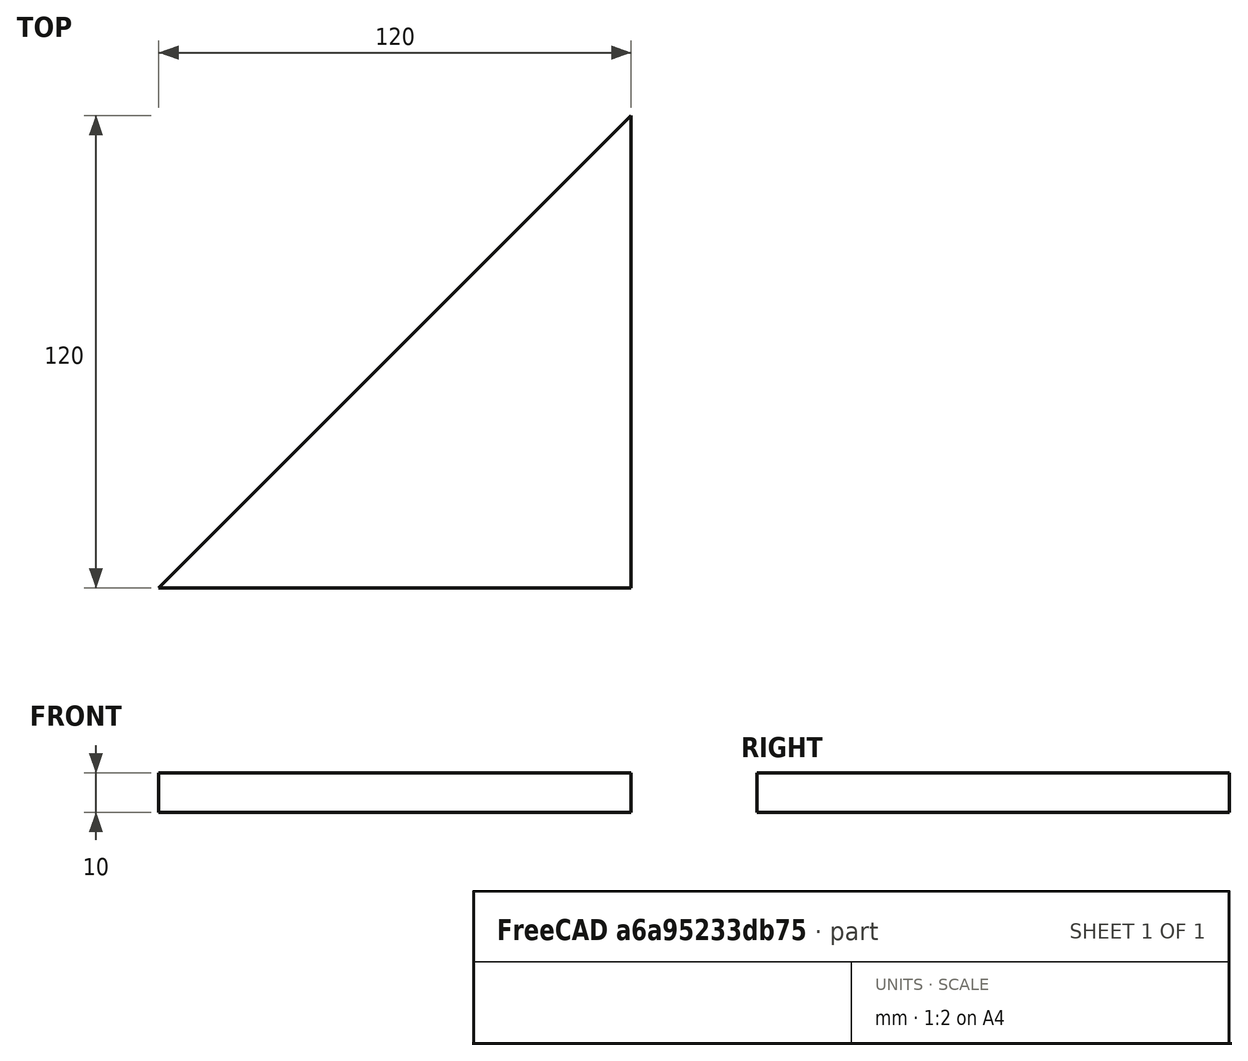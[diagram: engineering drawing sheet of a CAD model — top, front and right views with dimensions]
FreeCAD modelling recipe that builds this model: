
FCSTD DOCUMENT  (FreeCAD 0.14R3702 (Git))
Label: Base_SoporteMotor
License: CC-BY 3.0
LicenseURL: http://creativecommons.org/licenses/by/3.0/
objects: Sketcher::SketchObject×1, PartDesign::Pad×1
note: 3 computed .brp shape members not serialized (recipe doc carries the construction recipe); baked Part::Feature solids carry a one-line shape summary decoded from their .brp

FEATURE [Sketcher::SketchObject] Sketch
  sketch-geometry (3):
    g0: LineSegment StartX=-38.0492 StartY=-61.9463 StartZ=0 EndX=81.9508 EndY=-61.9463 EndZ=0
    g1: LineSegment StartX=81.9508 StartY=-61.9463 StartZ=0 EndX=81.9508 EndY=58.0537 EndZ=0
    g2: LineSegment StartX=81.9508 StartY=58.0537 StartZ=0 EndX=-38.0492 EndY=-61.9463 EndZ=0
  constraints (7):
    c: Horizontal(g0)
    c: Coincident(g1,g0)
    c: Vertical(g1)
    c: Coincident(g2,g1)
    c: Coincident(g2,g0)
    c: DistanceX(g0,g0) = 120
    c: DistanceY(g0,g1) = 120
FEATURE [PartDesign::Pad] Pad
  Length = 10
  Length2 = 100
  Sketch = -> Sketch
  Type = 0
